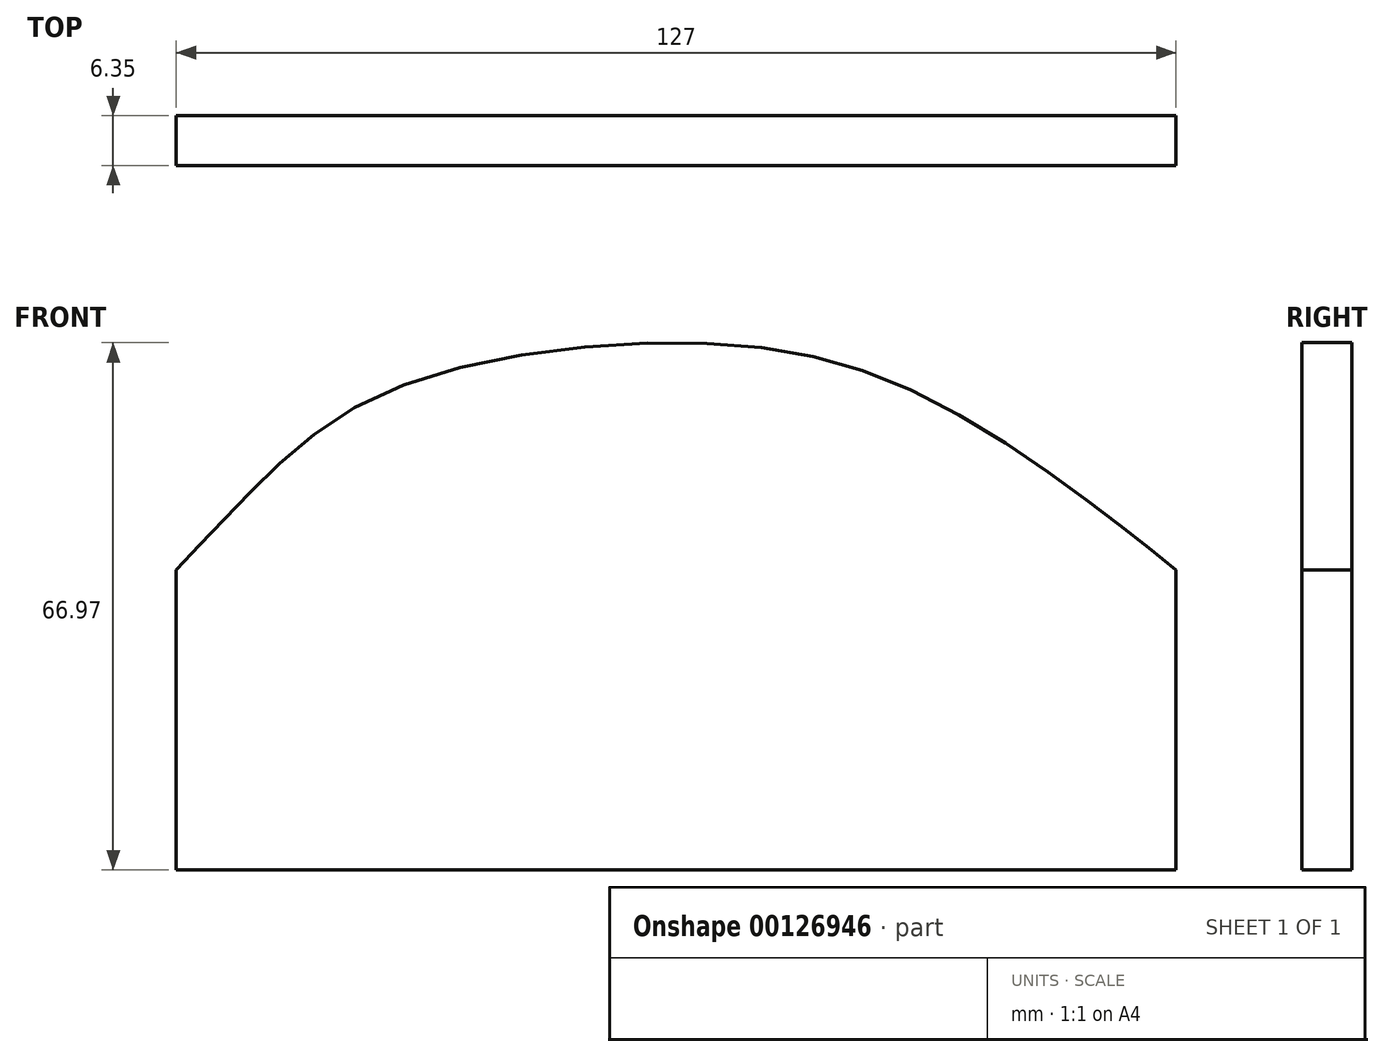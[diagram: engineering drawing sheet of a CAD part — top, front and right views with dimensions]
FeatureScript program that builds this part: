
annotation { "Feature Type Name" : "Feature", "Feature Type Description" : "" }
export const myFeature = defineFeature(function(context is Context, id is Id, definition is map)
    precondition{}
    {
        {
            var Q0;
            Q0=qCreatedBy(makeId("Front.planeOp"),FACE);
            var sketch = newSketch(context, id + "F0", { "sketchPlane" : qUnion([Q0])});
            skLineSegment(sketch, "E0.top", {"start": v(63.5, -38.1) * mm, "end": v(-63.5, -38.1) * mm});
            skLineSegment(sketch, "E0.left", {"start": v(63.5, 0) * mm, "end": v(63.5, -38.1) * mm});
            skLineSegment(sketch, "E0.right", {"start": v(-63.5, 0) * mm, "end": v(-63.5, -38.1) * mm});
            skPoint(sketch, "E0.middle", {"position": v(0, 0) * mm});
            skFitSpline(sketch, "E1", {"points": [v(-63.5, 0) * mm, v(-54.53, 9.41) * mm, v(-37.58, 22.28) * mm, v(0, 28.87) * mm, v(28.3, 23.53) * mm, v(51.84, 9.1) * mm, v(63.5, 0) * mm], "startDerivative": vector(67.9, 72.11) * mm, "endDerivative": vector(78.71, -63.38) * mm});
            skPoint(sketch, "E2.orphan", {"position": v(-63.5, 38.1) * mm});
            skPoint(sketch, "E3.orphan", {"position": v(63.5, 38.1) * mm});
            skSolve(sketch);
        }
        {
            var Q0;
            Q0=makeQuery(id+"F0.imprint","IMPRINT",FACE,{"disambiguationData":[TD([[makeQuery(id+"F0.imprint","IMPRINT",EDGE,{"derivedFrom":sQuery(id+"F0.wireOp",EDGE,"E0.top")}),-1.0]])]});
            extrude(context, id + "F1", {"entities" : qUnion([Q0]), "depth" : 6.35 * mm});
        }
    });
